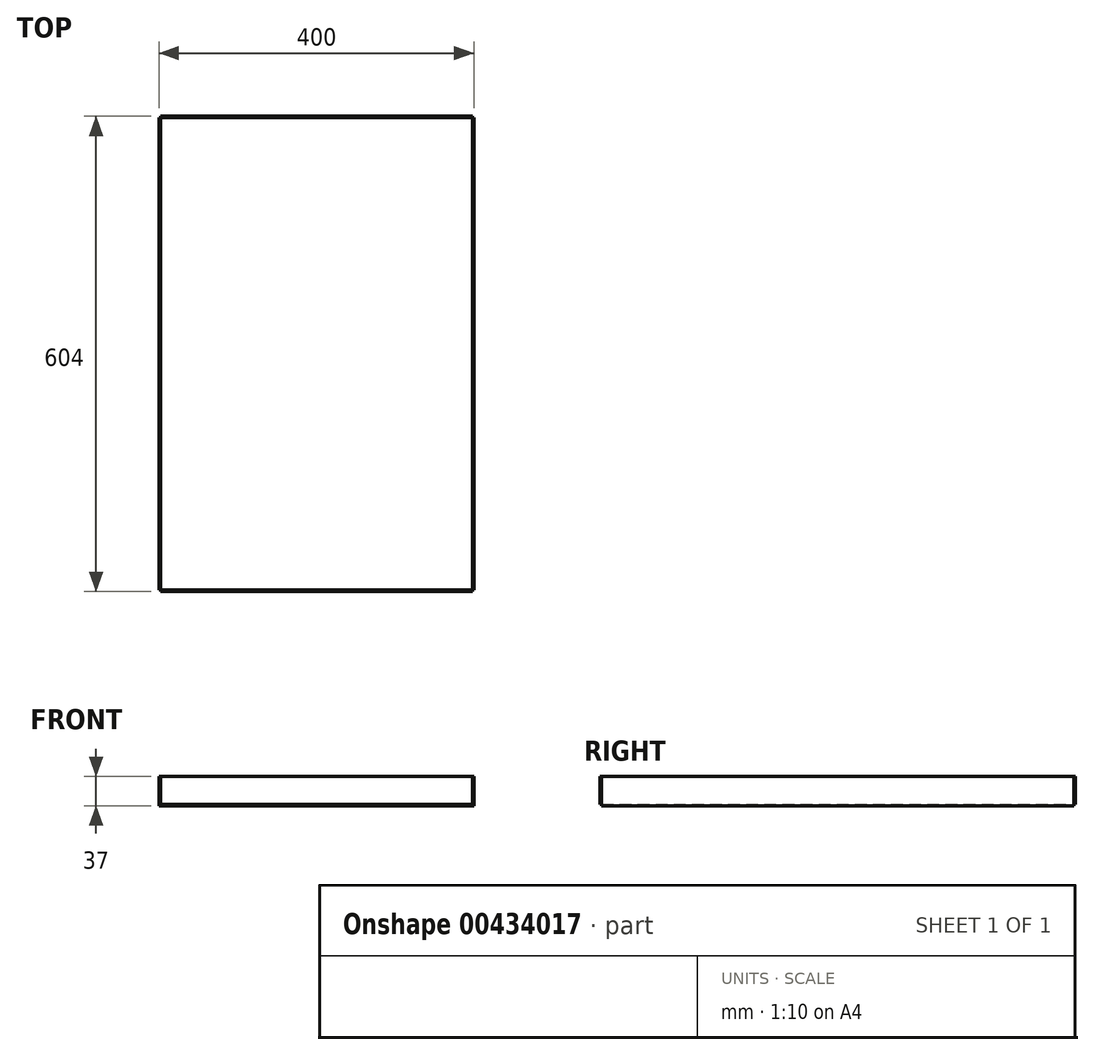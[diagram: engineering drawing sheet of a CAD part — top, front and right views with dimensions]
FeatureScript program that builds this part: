
annotation { "Feature Type Name" : "Feature", "Feature Type Description" : "" }
export const myFeature = defineFeature(function(context is Context, id is Id, definition is map)
    precondition{}
    {
        {
            var Q0;
            Q0=qCreatedBy(makeId("Front.planeOp"),FACE);
            var sketch = newSketch(context, id + "F0", { "sketchPlane" : qUnion([Q0])});
            skLineSegment(sketch, "E0.bottom", {"start": v(-588.9, -5.24) * mm, "end": v(-192.9, -5.24) * mm});
            skLineSegment(sketch, "E0.top", {"start": v(-590.9, -7.24) * mm, "end": v(-190.9, -7.24) * mm});
            skLineSegment(sketch, "E0.left", {"start": v(-590.9, -5.24) * mm, "end": v(-590.9, -7.24) * mm});
            skLineSegment(sketch, "E0.right", {"start": v(-190.9, -5.24) * mm, "end": v(-190.9, -7.24) * mm});
            skLineSegment(sketch, "E1.top", {"start": v(-590.9, 29.76) * mm, "end": v(-588.9, 29.76) * mm});
            skLineSegment(sketch, "E1.left", {"start": v(-590.9, -5.24) * mm, "end": v(-590.9, 29.76) * mm});
            skLineSegment(sketch, "E1.right", {"start": v(-588.9, -5.24) * mm, "end": v(-588.9, 29.76) * mm});
            skLineSegment(sketch, "E2.top", {"start": v(-190.9, 29.76) * mm, "end": v(-192.9, 29.76) * mm});
            skLineSegment(sketch, "E2.left", {"start": v(-190.9, -5.24) * mm, "end": v(-190.9, 29.76) * mm});
            skLineSegment(sketch, "E2.right", {"start": v(-192.9, -5.24) * mm, "end": v(-192.9, 29.76) * mm});
            skSolve(sketch);
        }
        {
            var Q0;
            Q0=makeQuery(id+"F0.imprint","IMPRINT",FACE,{"disambiguationData":[TD([[makeQuery(id+"F0.imprint","IMPRINT",EDGE,{"derivedFrom":sQuery(id+"F0.wireOp",EDGE,"E0.bottom")}),-1.0]])]});
            extrude(context, id + "F1", {"entities" : qUnion([Q0]), "depth" : 600 * mm, "offsetDistance" : 25 * mm});
        }
        {
            var Q0;
            Q0=makeQuery(id+"F1.opExtrude","CAP_FACE",FACE,{"disambiguationData":[OSD([sQuery(id+"F0.wireOp",EDGE,"E0.bottom"),sQuery(id+"F0.wireOp",EDGE,"E0.top"),sQuery(id+"F0.wireOp",EDGE,"E0.left"),sQuery(id+"F0.wireOp",EDGE,"E0.right"),sQuery(id+"F0.wireOp",EDGE,"E1.top"),sQuery(id+"F0.wireOp",EDGE,"E1.left"),sQuery(id+"F0.wireOp",EDGE,"E1.right"),sQuery(id+"F0.wireOp",EDGE,"E2.top"),sQuery(id+"F0.wireOp",EDGE,"E2.left"),sQuery(id+"F0.wireOp",EDGE,"E2.right")])],"isStart":false});
            var sketch = newSketch(context, id + "F2", { "sketchPlane" : qUnion([Q0])});
            skLineSegment(sketch, "E3.bottom", {"start": v(-590.9, 29.76) * mm, "end": v(-192.9, 29.76) * mm});
            skLineSegment(sketch, "E3.top", {"start": v(-590.9, -5.24) * mm, "end": v(-192.9, -5.24) * mm});
            skLineSegment(sketch, "E3.left", {"start": v(-590.9, 29.76) * mm, "end": v(-590.9, -5.24) * mm});
            skLineSegment(sketch, "E3.right", {"start": v(-192.9, 29.76) * mm, "end": v(-192.9, -5.24) * mm});
            skSolve(sketch);
        }
        {
            var Q0;
            {var subQ2=sQuery(id+"F2.wireOp",EDGE,"E3.right");Q0=makeQuery(id+"F2.imprint","IMPRINT",FACE,{"disambiguationData":[TD([[makeQuery(id+"F2.imprint","IMPRINT",EDGE,{"derivedFrom":subQ2}),1.0]])]});}
            extrude(context, id + "F3", {"entities" : qUnion([Q0]), "depth" : 2 * mm, "offsetDistance" : 25 * mm});
        }
        {
            var Q0;
            Q0=makeQuery(id+"F1.opExtrude","CAP_FACE",FACE,{"disambiguationData":[OSD([sQuery(id+"F0.wireOp",EDGE,"E0.bottom"),sQuery(id+"F0.wireOp",EDGE,"E0.top"),sQuery(id+"F0.wireOp",EDGE,"E0.left"),sQuery(id+"F0.wireOp",EDGE,"E0.right"),sQuery(id+"F0.wireOp",EDGE,"E1.top"),sQuery(id+"F0.wireOp",EDGE,"E1.left"),sQuery(id+"F0.wireOp",EDGE,"E1.right"),sQuery(id+"F0.wireOp",EDGE,"E2.top"),sQuery(id+"F0.wireOp",EDGE,"E2.left"),sQuery(id+"F0.wireOp",EDGE,"E2.right")])],"isStart":true});
            var sketch = newSketch(context, id + "F4", { "sketchPlane" : qUnion([Q0])});
            skLineSegment(sketch, "E4.bottom", {"start": v(190.9, 29.76) * mm, "end": v(590.9, 29.76) * mm});
            skLineSegment(sketch, "E4.top", {"start": v(190.9, -7.24) * mm, "end": v(590.9, -7.24) * mm});
            skLineSegment(sketch, "E4.left", {"start": v(190.9, 29.76) * mm, "end": v(190.9, -7.24) * mm});
            skLineSegment(sketch, "E4.right", {"start": v(590.9, 29.76) * mm, "end": v(590.9, -7.24) * mm});
            skSolve(sketch);
        }
        {
            var Q0;
            Q0=makeQuery(id+"F4.imprint","IMPRINT",FACE,{"disambiguationData":[TD([[makeQuery(id+"F4.imprint","IMPRINT",EDGE,{"derivedFrom":makeQuery(id+"F1.opExtrude","CAP_EDGE",EDGE,{"disambiguationData":[OSD([sQuery(id+"F0.wireOp",EDGE,"E0.bottom")])],"isStart":true})}),-1.0]])]});
            extrude(context, id + "F5", {"entities" : qUnion([Q0]), "depth" : 2 * mm, "offsetDistance" : 25 * mm});
        }
    });
